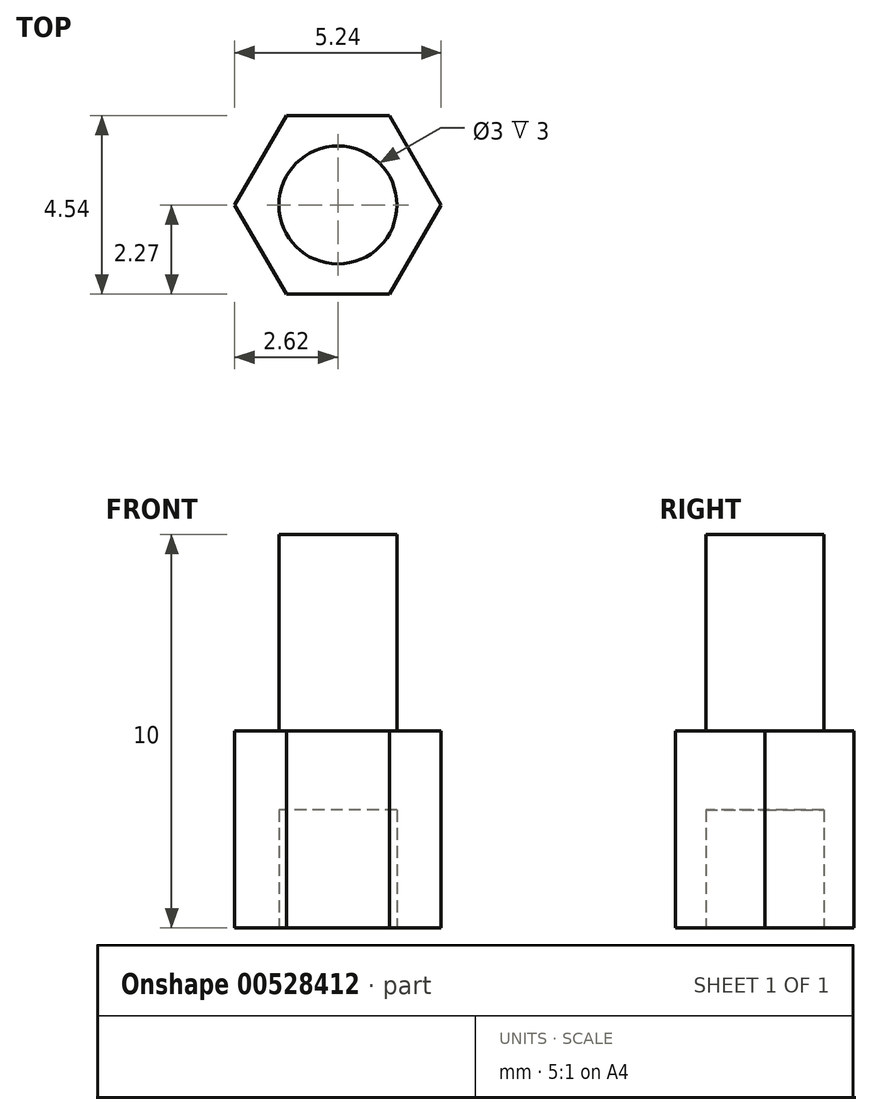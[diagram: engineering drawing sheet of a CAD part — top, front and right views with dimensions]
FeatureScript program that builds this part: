
annotation { "Feature Type Name" : "Feature", "Feature Type Description" : "" }
export const myFeature = defineFeature(function(context is Context, id is Id, definition is map)
    precondition{}
    {
        {
            var Q0;
            Q0=qCreatedBy(makeId("Top.planeOp"),FACE);
            var sketch = newSketch(context, id + "F0", { "sketchPlane" : qUnion([Q0])});
            skCircle(sketch, "E0", {"center": v(0, 0) * mm, "radius": 1.5 * mm});
            skCircle(sketch, "E1.cCircle", {"center": v(0, 0) * mm, "radius": 2.27 * mm, "construction": true});
            skLineSegment(sketch, "E1.0", {"start": v(-1.31, 2.27) * mm, "end": v(1.31, 2.27) * mm});
            skLineSegment(sketch, "E1.1", {"start": v(1.31, 2.27) * mm, "end": v(2.62, 0) * mm});
            skLineSegment(sketch, "E1.2", {"start": v(2.62, 0) * mm, "end": v(1.31, -2.27) * mm});
            skLineSegment(sketch, "E1.3", {"start": v(1.31, -2.27) * mm, "end": v(-1.31, -2.27) * mm});
            skLineSegment(sketch, "E1.4", {"start": v(-1.31, -2.27) * mm, "end": v(-2.62, 0) * mm});
            skLineSegment(sketch, "E1.5", {"start": v(-2.62, 0) * mm, "end": v(-1.31, 2.27) * mm});
            skPoint(sketch, "E1.0.midPoint", {"position": v(0, 2.27) * mm});
            skSolve(sketch);
        }
        {
            var Q0;
            Q0=makeQuery(id+"F0.imprint","IMPRINT",FACE,{"disambiguationData":[TD([[makeQuery(id+"F0.imprint","IMPRINT",EDGE,{"derivedFrom":sQuery(id+"F0.wireOp",EDGE,"E0")}),1.0]])]});
            extrude(context, id + "F1", {"entities" : qUnion([Q0]), "depth" : 10 * mm, "offsetDistance" : 25 * mm});
        }
        {
            var Q0;
            Q0=makeQuery(id+"F0.imprint","IMPRINT",FACE,{"disambiguationData":[TD([[makeQuery(id+"F0.imprint","IMPRINT",EDGE,{"derivedFrom":sQuery(id+"F0.wireOp",EDGE,"E0")}),-1.0]])]});
            extrude(context, id + "F2", {"entities" : qUnion([Q0]), "operationType" : NewBodyOperationType.ADD, "depth" : 5 * mm, "offsetDistance" : 25 * mm});
        }
        {
            var Q0;
            Q0=makeQuery(id+"F0.imprint","IMPRINT",FACE,{"disambiguationData":[TD([[makeQuery(id+"F0.imprint","IMPRINT",EDGE,{"derivedFrom":sQuery(id+"F0.wireOp",EDGE,"E0")}),1.0]])]});
            extrude(context, id + "F3", {"entities" : qUnion([Q0]), "operationType" : NewBodyOperationType.REMOVE, "depth" : 3 * mm, "offsetDistance" : 25 * mm});
        }
    });
